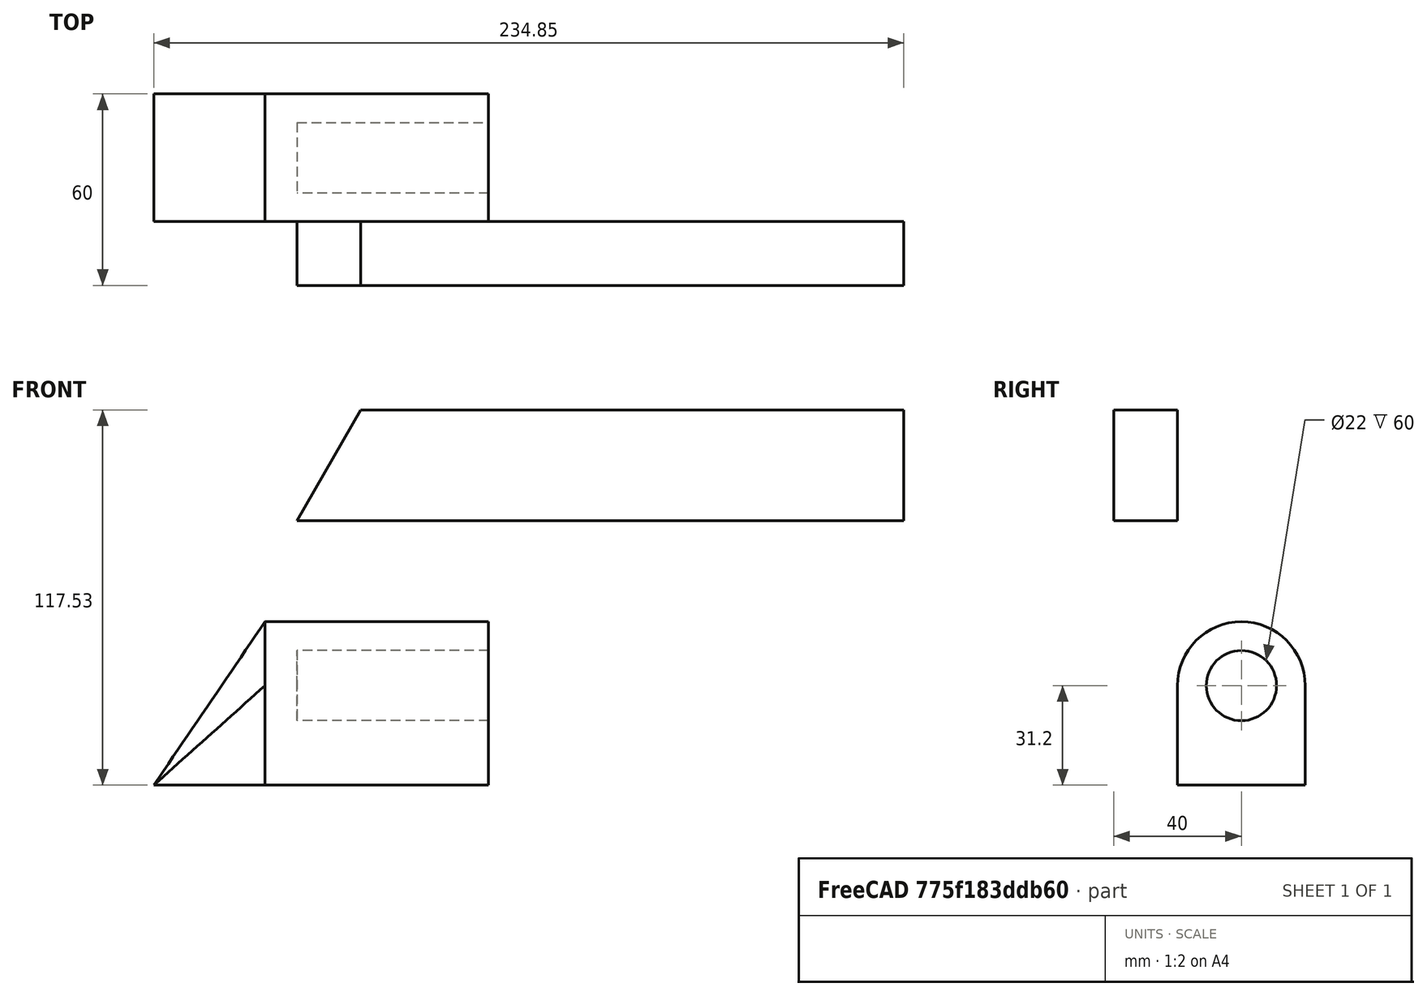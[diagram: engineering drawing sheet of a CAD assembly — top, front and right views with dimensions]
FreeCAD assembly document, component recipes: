
FREECAD ASSEMBLY — COMPONENT RECIPES ("Tagger3_test")

This assembly document has 2 components, labeled P0..P1 below (a component is one placed body or linked part). 2 of them carry a construction recipe — the FreeCAD feature program that regenerates the part from scratch, quoted from this document or its linked companion documents; the rest are supplied as boundary geometry only. No exploded tour is included for this assembly.
COMPONENT P0 — recipe-attached ("Barrel_left001", modeled in this document).
Construction recipe (the document's own serialized feature program — sketch geometry with constraints, then the solid features built on it; lengths are millimeters unless a unit is written):

FEATURE [Sketcher::SketchObject] Sketch
  FullyConstrained = false
  MapMode = 5
  Placement = pos=(0,0,0) rot=(1,0,0;1.5708rad)
  sketch-geometry (4):
    g0: LineSegment StartX=0 StartY=82.8841 StartZ=0 EndX=20 EndY=117.525 EndZ=0
    g1: LineSegment StartX=20 StartY=117.525 StartZ=0 EndX=190 EndY=117.525 EndZ=0
    g2: LineSegment StartX=190 StartY=117.525 StartZ=0 EndX=190 EndY=82.8841 EndZ=0
    g3: LineSegment StartX=0 StartY=82.8841 StartZ=0 EndX=190 EndY=82.8841 EndZ=0
  constraints (11):
    c: Coincident(g0,g1)
    c: Horizontal(g1)
    c: Coincident(g1,g2)
    c: Vertical(g2)
    c: Distance(g0,g0) = 40
    c: DistanceX(g1,g1) = 170
    c: Horizontal(g3)
    c: Coincident(g3,g2)
    c: Coincident(g3,g0)
    c: PointOnObject(g0,g-2)
    c: Angle(g3,g0) = 1.0472
FEATURE [PartDesign::Pad] Pad
  Direction = (0,-1,2e-16)
  Length = 20
  Length2 = 10
  Placement = pos=(0,0,0) rot=(1,0,0;1.5708rad)
  Profile = -> Sketch
  ReferenceAxis = -> Sketch [N_Axis]
  Refine = true
  Type = 0
FEATURE [PartDesign::Body] Body  label="Barrel_left"
  Group = -> [Sketch,Pad]
  Origin = -> Origin001
  Tip = -> Pad
COMPONENT P1 — recipe-attached ("Grip002", modeled in this document).
Construction recipe (the document's own serialized feature program — sketch geometry with constraints, then the solid features built on it; lengths are millimeters unless a unit is written):

FEATURE [Sketcher::SketchObject] Sketch002
  FullyConstrained = false
  MapMode = 5
  Placement = pos=(0,0,0) rot=(0.57735,0.57735,0.57735;2.0944rad)
  sketch-geometry (5):
    g0: LineSegment StartX=0 StartY=0 StartZ=0 EndX=40 EndY=0 EndZ=0
    g1: LineSegment StartX=40 StartY=0 StartZ=0 EndX=40 EndY=31.2 EndZ=0
    g2: LineSegment StartX=0 StartY=0 StartZ=0 EndX=0 EndY=31.2 EndZ=0
    g3: Circle CenterX=20 CenterY=31.2 CenterZ=0 NormalX=0 NormalY=0 NormalZ=1 AngleXU=0 Radius=11
    g4: ArcOfCircle CenterX=20 CenterY=31.2 CenterZ=0 NormalX=0 NormalY=0 NormalZ=1 AngleXU=0 Radius=20 StartAngle=0 EndAngle=3.14159
  constraints (12):
    c: Coincident(g0,g-1)
    c: PointOnObject(g0,g-1)
    c: Coincident(g1,g0)
    c: Vertical(g1)
    c: Coincident(g2,g0)
    c: PointOnObject(g2,g-2)
    c: Coincident(g4,g1)
    c: Diameter(g3) = 22
    c: Coincident(g4,g3)
    c: DistanceX(g0,g0) = 40
    c: Tangent(g4,g2) = 1.5708
    c: Equal(g1,g2)
FEATURE [PartDesign::Pad] Pad002
  Direction = (1,0,0)
  Length = 60
  Length2 = 10
  Placement = pos=(0,0,0) rot=(0.57735,0.57735,0.57735;2.0944rad)
  Profile = -> Sketch002
  ReferenceAxis = -> Sketch002 [N_Axis]
  Refine = true
  Type = 0
FEATURE [Sketcher::SketchObject] Sketch004
  ExternalGeometry = -> [Pad002,Sketch002]
  FullyConstrained = true
  MapMode = 5
  Placement = pos=(0,0,0) rot=(0.57735,0.57735,0.57735;2.0944rad)
  sketch-geometry (4):
    g0: LineSegment StartX=40 StartY=0 StartZ=0 EndX=40 EndY=31.2 EndZ=0
    g1: LineSegment StartX=40 StartY=0 StartZ=0 EndX=0 EndY=0 EndZ=0
    g2: LineSegment StartX=0 StartY=0 StartZ=0 EndX=1.07e-14 EndY=31.2 EndZ=0
    g3: ArcOfCircle CenterX=20 CenterY=31.2 CenterZ=0 NormalX=0 NormalY=0 NormalZ=1 AngleXU=0 Radius=20 StartAngle=0 EndAngle=3.14159
  constraints (9):
    c: Coincident(g0,g-3)
    c: Coincident(g1,g0)
    c: Coincident(g1,g-1)
    c: Coincident(g2,g1)
    c: Coincident(g3,g2)
    c: Coincident(g2,g-5)
    c: Coincident(g3,g0)
    c: Coincident(g0,g-5)
    c: Coincident(g3,g-5)
FEATURE [PartDesign::Pad] Pad003
  BaseFeature = -> Pad002
  Direction = (1,0,0)
  Length = 10
  Length2 = 10
  Placement = pos=(0,0,0) rot=(0.57735,0.57735,0.57735;2.0944rad)
  Profile = -> Sketch004
  ReferenceAxis = -> Sketch004 [N_Axis]
  Refine = true
  Reversed = true
  Type = 0
FEATURE [Sketcher::SketchObject] Sketch003
  ExternalGeometry = -> [Pad003]
  FullyConstrained = false
  MapMode = 5
  sketch-geometry (4):
    g0: LineSegment StartX=-10 StartY=40 StartZ=0 EndX=-44.8526 EndY=40 EndZ=0
    g1: LineSegment StartX=-44.8526 StartY=40 StartZ=0 EndX=-44.8526 EndY=0 EndZ=0
    g2: LineSegment StartX=-44.8526 StartY=0 StartZ=0 EndX=-10 EndY=0 EndZ=0
    g3: LineSegment StartX=-10 StartY=0 StartZ=0 EndX=-10 EndY=40 EndZ=0
  constraints (10):
    c: Coincident(g0,g1)
    c: Coincident(g1,g2)
    c: Coincident(g2,g3)
    c: Coincident(g3,g0)
    c: Horizontal(g0)
    c: Horizontal(g2)
    c: Vertical(g1)
    c: Vertical(g3)
    c: PointOnObject(g1,g-1)
    c: Coincident(g0,g-3)
FEATURE [PartDesign::AdditiveLoft] AdditiveLoft
  BaseFeature = -> Pad003
  Closed = false
  Placement = pos=(0,0,0) rot=(0.57735,0.57735,0.57735;2.0944rad)
  Profile = -> Sketch003
  Refine = true
  Ruled = false
  Sections = -> [Pad003]
FEATURE [PartDesign::Body] Body002  label="Grip2"
  Group = -> [Sketch002,Pad002,Sketch003,Sketch004,Pad003,AdditiveLoft]
  Origin = -> Origin003
  Tip = -> AdditiveLoft
PROVENANCE & LICENSES
A FreeCAD (.FCStd) document from a public repository crawl; recipes are the document's own serialized feature recipes (and, for linked parts, companion documents' recipes).
License: bsd.
